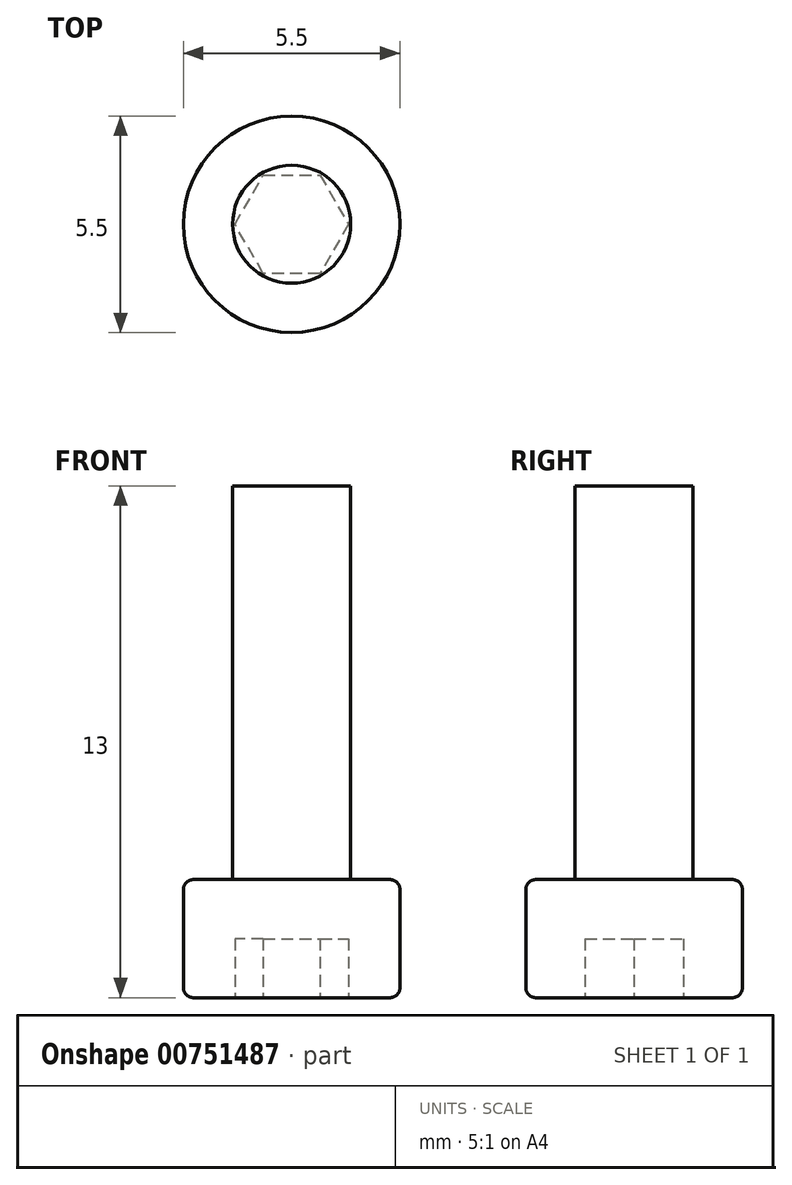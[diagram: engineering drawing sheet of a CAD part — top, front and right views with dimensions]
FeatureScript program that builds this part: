
annotation { "Feature Type Name" : "Feature", "Feature Type Description" : "" }
export const myFeature = defineFeature(function(context is Context, id is Id, definition is map)
    precondition{}
    {
        {
            assignVariable(context, id + "F0", {"name" : "ShaftLength", "anyValue" : 10});
        }
        {
            var Q0;
            Q0=qCreatedBy(makeId("Top.planeOp"),FACE);
            var sketch = newSketch(context, id + "F1", { "sketchPlane" : qUnion([Q0])});
            skCircle(sketch, "E0", {"center": v(0, 0) * mm, "radius": 2.75 * mm});
            skCircle(sketch, "E1.cCircle", {"center": v(0, 0) * mm, "radius": 1.25 * mm, "construction": true});
            skLineSegment(sketch, "E1.0", {"start": v(-1.44, 0) * mm, "end": v(-0.72, 1.25) * mm});
            skLineSegment(sketch, "E1.1", {"start": v(-0.72, 1.25) * mm, "end": v(0.72, 1.25) * mm});
            skLineSegment(sketch, "E1.2", {"start": v(0.72, 1.25) * mm, "end": v(1.44, 0) * mm});
            skLineSegment(sketch, "E1.3", {"start": v(1.44, 0) * mm, "end": v(0.72, -1.25) * mm});
            skLineSegment(sketch, "E1.4", {"start": v(0.72, -1.25) * mm, "end": v(-0.72, -1.25) * mm});
            skLineSegment(sketch, "E1.5", {"start": v(-0.72, -1.25) * mm, "end": v(-1.44, 0) * mm});
            skPoint(sketch, "E1.0.midPoint", {"position": v(-1.08, 0.62) * mm});
            skCircle(sketch, "E2", {"center": v(0, 0) * mm, "radius": 1.5 * mm});
            skSolve(sketch);
        }
        {
            var Q0;
            Q0=makeQuery(id+"F1.imprint","IMPRINT",FACE,{"disambiguationData":[TD([[makeQuery(id+"F1.imprint","IMPRINT",EDGE,{"derivedFrom":sQuery(id+"F1.wireOp",EDGE,"E0")}),1.0]])]});
            var Q1;
            Q1=makeQuery(id+"F1.imprint","IMPRINT",FACE,{"disambiguationData":[TD([[makeQuery(id+"F1.imprint","IMPRINT",EDGE,{"derivedFrom":sQuery(id+"F1.wireOp",EDGE,"E1.0")}),1.0]])]});
            extrude(context, id + "F2", {"entities" : qUnion([Q0, Q1]), "depth" : 3 * mm, "offsetDistance" : 25 * mm});
        }
        {
            var Q0;
            {var subQ0=sQuery(id+"F1.wireOp",EDGE,"E1.5");var subQ1=sQuery(id+"F1.wireOp",EDGE,"E1.4");var subQ2=makeQuery(id+"F1.imprint","INTERSECT",VERTEX,{"derivedFrom":[subQ1,subQ0]});Q0=makeQuery(id+"F1.imprint","IMPRINT",FACE,{"disambiguationData":[TD([[makeQuery(id+"F1.imprint","IMPRINT",EDGE,{"disambiguationData":[TD([[subQ2,1.0]])],"derivedFrom":subQ1}),-1.0]])]});}
            var Q1;
            {var subQ0=sQuery(id+"F1.wireOp",EDGE,"E1.4");var subQ1=sQuery(id+"F1.wireOp",EDGE,"E1.3");var subQ2=makeQuery(id+"F1.imprint","INTERSECT",VERTEX,{"derivedFrom":[subQ1,subQ0]});Q1=makeQuery(id+"F1.imprint","IMPRINT",FACE,{"disambiguationData":[TD([[makeQuery(id+"F1.imprint","IMPRINT",EDGE,{"disambiguationData":[TD([[subQ2,1.0]])],"derivedFrom":subQ1}),-1.0]])]});}
            var Q2;
            {var subQ0=sQuery(id+"F1.wireOp",EDGE,"E1.5");var subQ1=sQuery(id+"F1.wireOp",EDGE,"E1.0");var subQ2=makeQuery(id+"F1.imprint","INTERSECT",VERTEX,{"derivedFrom":[subQ1,subQ0]});Q2=makeQuery(id+"F1.imprint","IMPRINT",FACE,{"disambiguationData":[TD([[makeQuery(id+"F1.imprint","IMPRINT",EDGE,{"disambiguationData":[TD([[subQ2,-1.0]])],"derivedFrom":subQ1}),-1.0]])]});}
            var Q3;
            {var subQ0=sQuery(id+"F1.wireOp",EDGE,"E2");var subQ4=makeQuery(id+"F1.imprint","INTERSECT",VERTEX,{"derivedFrom":[sQuery(id+"F1.wireOp",EDGE,"E1.1"),subQ0]});Q3=makeQuery(id+"F1.imprint","IMPRINT",FACE,{"disambiguationData":[TD([[makeQuery(id+"F1.imprint","IMPRINT",EDGE,{"disambiguationData":[TD([[subQ4,1.0]])],"derivedFrom":subQ0}),1.0]])]});}
            var Q4;
            {var subQ0=sQuery(id+"F1.wireOp",EDGE,"E1.1");var subQ1=sQuery(id+"F1.wireOp",EDGE,"E1.0");var subQ2=makeQuery(id+"F1.imprint","INTERSECT",VERTEX,{"derivedFrom":[subQ1,subQ0]});Q4=makeQuery(id+"F1.imprint","IMPRINT",FACE,{"disambiguationData":[TD([[makeQuery(id+"F1.imprint","IMPRINT",EDGE,{"disambiguationData":[TD([[subQ2,1.0]])],"derivedFrom":subQ1}),-1.0]])]});}
            var Q5;
            {var subQ0=sQuery(id+"F1.wireOp",EDGE,"E1.2");var subQ1=sQuery(id+"F1.wireOp",EDGE,"E1.1");var subQ2=makeQuery(id+"F1.imprint","INTERSECT",VERTEX,{"derivedFrom":[subQ1,subQ0]});Q5=makeQuery(id+"F1.imprint","IMPRINT",FACE,{"disambiguationData":[TD([[makeQuery(id+"F1.imprint","IMPRINT",EDGE,{"disambiguationData":[TD([[subQ2,1.0]])],"derivedFrom":subQ1}),-1.0]])]});}
            var Q6;
            {var subQ0=sQuery(id+"F1.wireOp",EDGE,"E1.3");var subQ1=sQuery(id+"F1.wireOp",EDGE,"E1.2");var subQ2=makeQuery(id+"F1.imprint","INTERSECT",VERTEX,{"derivedFrom":[subQ1,subQ0]});Q6=makeQuery(id+"F1.imprint","IMPRINT",FACE,{"disambiguationData":[TD([[makeQuery(id+"F1.imprint","IMPRINT",EDGE,{"disambiguationData":[TD([[subQ2,1.0]])],"derivedFrom":subQ1}),-1.0]])]});}
            extrude(context, id + "F3", {"entities" : qUnion([Q0, Q1, Q2, Q3, Q4, Q5, Q6]), "operationType" : NewBodyOperationType.ADD, "depth" : 3 * mm, "offsetDistance" : 25 * mm, "hasSecondDirection" : true, "secondDirectionOppositeDirection" : false, "secondDirectionDepth" : 1.5 * mm});
        }
        {
            var Q0;
            {var subQ0=sQuery(id+"F1.wireOp",EDGE,"E2");var subQ4=makeQuery(id+"F1.imprint","INTERSECT",VERTEX,{"derivedFrom":[sQuery(id+"F1.wireOp",EDGE,"E1.1"),subQ0]});Q0=makeQuery(id+"F1.imprint","IMPRINT",FACE,{"disambiguationData":[TD([[makeQuery(id+"F1.imprint","IMPRINT",EDGE,{"disambiguationData":[TD([[subQ4,1.0]])],"derivedFrom":subQ0}),1.0]])]});}
            var Q1;
            Q1=makeQuery(id+"F1.imprint","IMPRINT",FACE,{"disambiguationData":[TD([[makeQuery(id+"F1.imprint","IMPRINT",EDGE,{"derivedFrom":sQuery(id+"F1.wireOp",EDGE,"E1.0")}),-1.0]])]});
            extrude(context, id + "F4", {"entities" : qUnion([Q0, Q1]), "operationType" : NewBodyOperationType.ADD, "depth" : (getVariable(context, 'ShaftLength') + 3) * mm, "offsetDistance" : 25 * mm, "hasSecondDirection" : true, "secondDirectionOppositeDirection" : false, "secondDirectionDepth" : 3 * mm});
        }
        {
            var Q0;
            Q0=makeQuery(id+"F2.opExtrude","CAP_EDGE",EDGE,{"disambiguationData":[OSD([sQuery(id+"F1.wireOp",EDGE,"E0")])],"isStart":false});
            var Q1;
            Q1=makeQuery(id+"F2.opExtrude","CAP_EDGE",EDGE,{"disambiguationData":[OSD([sQuery(id+"F1.wireOp",EDGE,"E0")])],"isStart":true});
            var Q2;
            Q2=makeQuery(id+"F4.opExtrude","CAP_EDGE",EDGE,{"disambiguationData":[OSD([sQuery(id+"F1.wireOp",EDGE,"E2")])],"isStart":true});
            fillet(context, id + "F5", {"entities" : qUnion([Q0, Q1, Q2]), "radius" : .25 * mm, "tangentPropagation" : true, "allowEdgeOverflow" : false});
        }
    });
